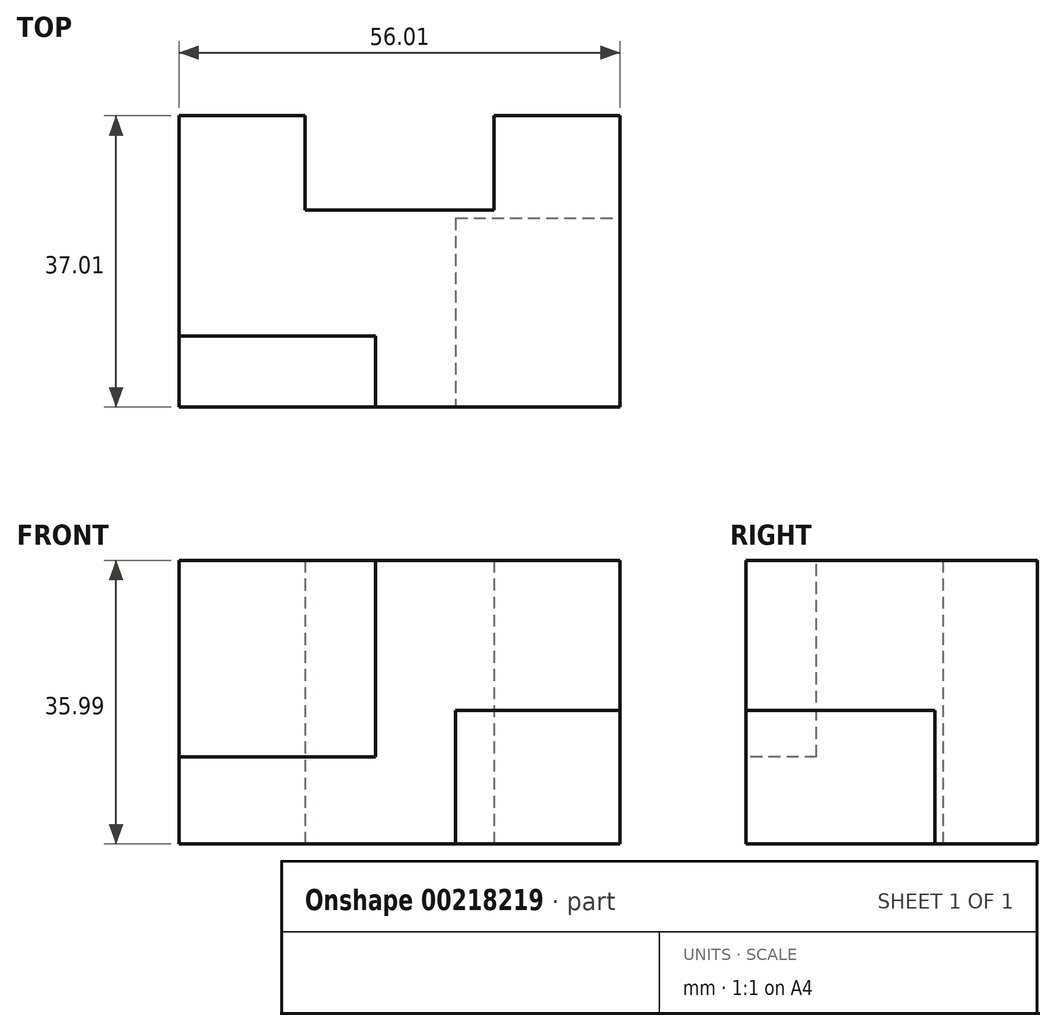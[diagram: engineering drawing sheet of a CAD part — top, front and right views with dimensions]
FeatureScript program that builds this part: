
annotation { "Feature Type Name" : "Feature", "Feature Type Description" : "" }
export const myFeature = defineFeature(function(context is Context, id is Id, definition is map)
    precondition{}
    {
        {
            var Q0;
            Q0=qCreatedBy(makeId("Top.planeOp"),FACE);
            var sketch = newSketch(context, id + "F0", { "sketchPlane" : qUnion([Q0])});
            skLineSegment(sketch, "E0.bottom", {"start": v(28.85, 64.73) * mm, "end": v(44.86, 64.73) * mm});
            skLineSegment(sketch, "E0.top", {"start": v(28.85, 27.72) * mm, "end": v(84.86, 27.72) * mm});
            skLineSegment(sketch, "E0.left", {"start": v(28.85, 64.73) * mm, "end": v(28.85, 27.72) * mm});
            skLineSegment(sketch, "E0.right", {"start": v(84.86, 64.73) * mm, "end": v(84.86, 27.72) * mm});
            skLineSegment(sketch, "E1.0", {"start": v(44.86, 64.73) * mm, "end": v(44.86, 52.74) * mm});
            skLineSegment(sketch, "E2.0", {"start": v(68.86, 64.73) * mm, "end": v(68.86, 52.74) * mm});
            skLineSegment(sketch, "E3.0", {"start": v(44.86, 52.74) * mm, "end": v(68.86, 52.74) * mm});
            skLineSegment(sketch, "E4.trimOffspring", {"start": v(68.86, 64.73) * mm, "end": v(84.86, 64.73) * mm});
            skSolve(sketch);
        }
        {
            var Q0;
            Q0=makeQuery(id+"F0.imprint","IMPRINT",FACE,{"disambiguationData":[TD([[makeQuery(id+"F0.imprint","IMPRINT",EDGE,{"derivedFrom":sQuery(id+"F0.wireOp",EDGE,"E0.bottom")}),-1.0]])]});
            extrude(context, id + "F1", {"entities" : qUnion([Q0]), "depth" : 36 * mm});
        }
        {
            var Q0;
            Q0=makeQuery(id+"F1.opExtrude","CAP_FACE",FACE,{"disambiguationData":[OSD([sQuery(id+"F0.wireOp",EDGE,"E0.bottom"),sQuery(id+"F0.wireOp",EDGE,"E0.top"),sQuery(id+"F0.wireOp",EDGE,"E0.left"),sQuery(id+"F0.wireOp",EDGE,"E0.right"),sQuery(id+"F0.wireOp",EDGE,"E1.0"),sQuery(id+"F0.wireOp",EDGE,"E2.0"),sQuery(id+"F0.wireOp",EDGE,"E3.0"),sQuery(id+"F0.wireOp",EDGE,"E4.trimOffspring")])],"isStart":false});
            var sketch = newSketch(context, id + "F2", { "sketchPlane" : qUnion([Q0])});
            skLineSegment(sketch, "E5.bottom", {"start": v(28.85, 27.72) * mm, "end": v(53.82, 27.72) * mm});
            skLineSegment(sketch, "E5.top", {"start": v(28.85, 36.71) * mm, "end": v(53.82, 36.71) * mm});
            skLineSegment(sketch, "E5.left", {"start": v(28.85, 27.72) * mm, "end": v(28.85, 36.71) * mm});
            skLineSegment(sketch, "E5.right", {"start": v(53.82, 27.72) * mm, "end": v(53.82, 36.71) * mm});
            skSolve(sketch);
        }
        {
            var Q0;
            Q0=makeQuery(id+"F2.imprint","IMPRINT",FACE,{"disambiguationData":[TD([[makeQuery(id+"F2.imprint","IMPRINT",EDGE,{"derivedFrom":sQuery(id+"F2.wireOp",EDGE,"E5.bottom")}),1.0]])]});
            extrude(context, id + "F3", {"entities" : qUnion([Q0]), "operationType" : NewBodyOperationType.REMOVE, "oppositeDirection" : true, "depth" : 24.94 * mm});
        }
        {
            var Q0;
            Q0=makeQuery(id+"F1.opExtrude","SWEPT_FACE",FACE,{"disambiguationData":[OSD([sQuery(id+"F0.wireOp",EDGE,"E0.top")])]});
            var sketch = newSketch(context, id + "F4", { "sketchPlane" : qUnion([Q0])});
            skLineSegment(sketch, "E6.bottom", {"start": v(84.86, 0) * mm, "end": v(64, 0) * mm});
            skLineSegment(sketch, "E6.top", {"start": v(84.86, 16.94) * mm, "end": v(64, 16.94) * mm});
            skLineSegment(sketch, "E6.left", {"start": v(84.86, 0) * mm, "end": v(84.86, 16.94) * mm});
            skLineSegment(sketch, "E6.right", {"start": v(64, 0) * mm, "end": v(64, 16.94) * mm});
            skSolve(sketch);
        }
        {
            var Q0;
            Q0=makeQuery(id+"F4.imprint","IMPRINT",FACE,{"disambiguationData":[TD([[makeQuery(id+"F4.imprint","IMPRINT",EDGE,{"derivedFrom":sQuery(id+"F4.wireOp",EDGE,"E6.bottom")}),1.0]])]});
            extrude(context, id + "F5", {"entities" : qUnion([Q0]), "operationType" : NewBodyOperationType.REMOVE, "oppositeDirection" : true, "depth" : 24 * mm});
        }
    });
